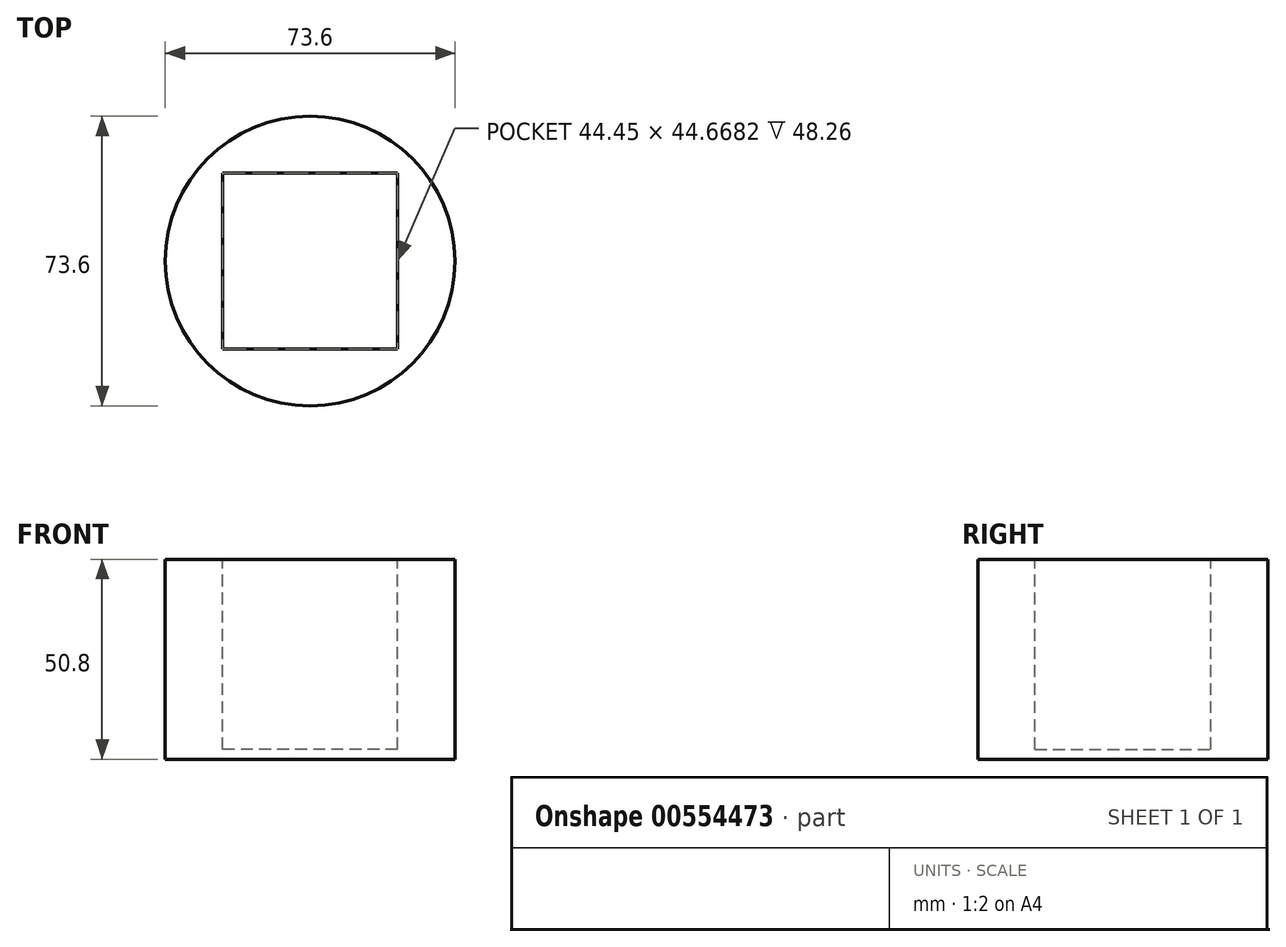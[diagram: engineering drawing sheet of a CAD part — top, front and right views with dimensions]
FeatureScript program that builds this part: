
annotation { "Feature Type Name" : "Feature", "Feature Type Description" : "" }
export const myFeature = defineFeature(function(context is Context, id is Id, definition is map)
    precondition{}
    {
        {
            var Q0;
            Q0=qCreatedBy(makeId("Top.planeOp"),FACE);
            var sketch = newSketch(context, id + "F0", { "sketchPlane" : qUnion([Q0])});
            skLineSegment(sketch, "E0.bottom", {"start": v(-25.4, 25.4) * mm, "end": v(25.4, 25.4) * mm});
            skLineSegment(sketch, "E0.top", {"start": v(-25.4, -25.4) * mm, "end": v(25.4, -25.4) * mm});
            skLineSegment(sketch, "E0.left", {"start": v(-25.4, 25.4) * mm, "end": v(-25.4, -25.4) * mm});
            skLineSegment(sketch, "E0.right", {"start": v(25.4, 25.4) * mm, "end": v(25.4, -25.4) * mm});
            skPoint(sketch, "E0.middle", {"position": v(0, 0) * mm});
            skSolve(sketch);
        }
        {
            var Q0;
            Q0=makeQuery(id+"F0.imprint","IMPRINT",FACE,{"disambiguationData":[TD([[makeQuery(id+"F0.imprint","IMPRINT",EDGE,{"derivedFrom":sQuery(id+"F0.wireOp",EDGE,"E0.bottom")}),-1.0]])]});
            extrude(context, id + "F1", {"entities" : qUnion([Q0]), "depth" : 50.8 * mm, "offsetDistance" : 25.4 * mm});
        }
        {
            var Q0;
            Q0=makeQuery(id+"F1.opExtrude","CAP_FACE",FACE,{"disambiguationData":[OSD([sQuery(id+"F0.wireOp",EDGE,"E0.bottom"),sQuery(id+"F0.wireOp",EDGE,"E0.top"),sQuery(id+"F0.wireOp",EDGE,"E0.left"),sQuery(id+"F0.wireOp",EDGE,"E0.right")])],"isStart":false});
            var sketch = newSketch(context, id + "F2", { "sketchPlane" : qUnion([Q0])});
            skLineSegment(sketch, "E1.bottom", {"start": v(22.23, -22.33) * mm, "end": v(-22.23, -22.33) * mm});
            skLineSegment(sketch, "E1.top", {"start": v(22.23, 22.33) * mm, "end": v(-22.23, 22.33) * mm});
            skLineSegment(sketch, "E1.left", {"start": v(22.23, -22.33) * mm, "end": v(22.23, 22.33) * mm});
            skLineSegment(sketch, "E1.right", {"start": v(-22.23, -22.33) * mm, "end": v(-22.23, 22.33) * mm});
            skPoint(sketch, "E1.middle", {"position": v(0, 0) * mm});
            skSolve(sketch);
        }
        {
            var Q0;
            Q0=makeQuery(id+"F2.imprint","IMPRINT",FACE,{"disambiguationData":[TD([[makeQuery(id+"F2.imprint","IMPRINT",EDGE,{"derivedFrom":sQuery(id+"F2.wireOp",EDGE,"E1.bottom")}),-1.0]])]});
            extrude(context, id + "F3", {"entities" : qUnion([Q0]), "operationType" : NewBodyOperationType.REMOVE, "oppositeDirection" : true, "depth" : 48.26 * mm, "offsetDistance" : 25.4 * mm});
        }
        {
            var Q0;
            Q0=qCreatedBy(makeId("Top.planeOp"),FACE);
            var sketch = newSketch(context, id + "F4", { "sketchPlane" : qUnion([Q0])});
            skCircle(sketch, "E2", {"center": v(0, 0) * mm, "radius": 36.8 * mm});
            skSolve(sketch);
        }
        {
            var Q0;
            Q0 = qSketchRegion(id + "F4", true);
            extrude(context, id + "F5", {"entities" : qUnion([Q0]), "operationType" : NewBodyOperationType.ADD, "depth" : 50.8 * mm, "offsetDistance" : 25.4 * mm});
        }
        {
            var Q0;
            Q0=makeQuery(id+"F2.imprint","IMPRINT",FACE,{"disambiguationData":[TD([[makeQuery(id+"F2.imprint","IMPRINT",EDGE,{"derivedFrom":sQuery(id+"F2.wireOp",EDGE,"E1.bottom")}),-1.0]])]});
            var sketch = newSketch(context, id + "F6", { "sketchPlane" : qUnion([Q0])});
            skSolve(sketch);
        }
        {
            var Q0;
            Q0 = qSketchRegion(id + "F6", true);
            var Q1;
            Q1=makeQuery(id+"F2.imprint","IMPRINT",FACE,{"disambiguationData":[TD([[makeQuery(id+"F2.imprint","IMPRINT",EDGE,{"derivedFrom":sQuery(id+"F2.wireOp",EDGE,"E1.bottom")}),-1.0]])]});
            extrude(context, id + "F7", {"entities" : qUnion([Q0, Q1]), "operationType" : NewBodyOperationType.REMOVE, "oppositeDirection" : true, "depth" : 48.26 * mm, "offsetDistance" : 25.4 * mm});
        }
    });
